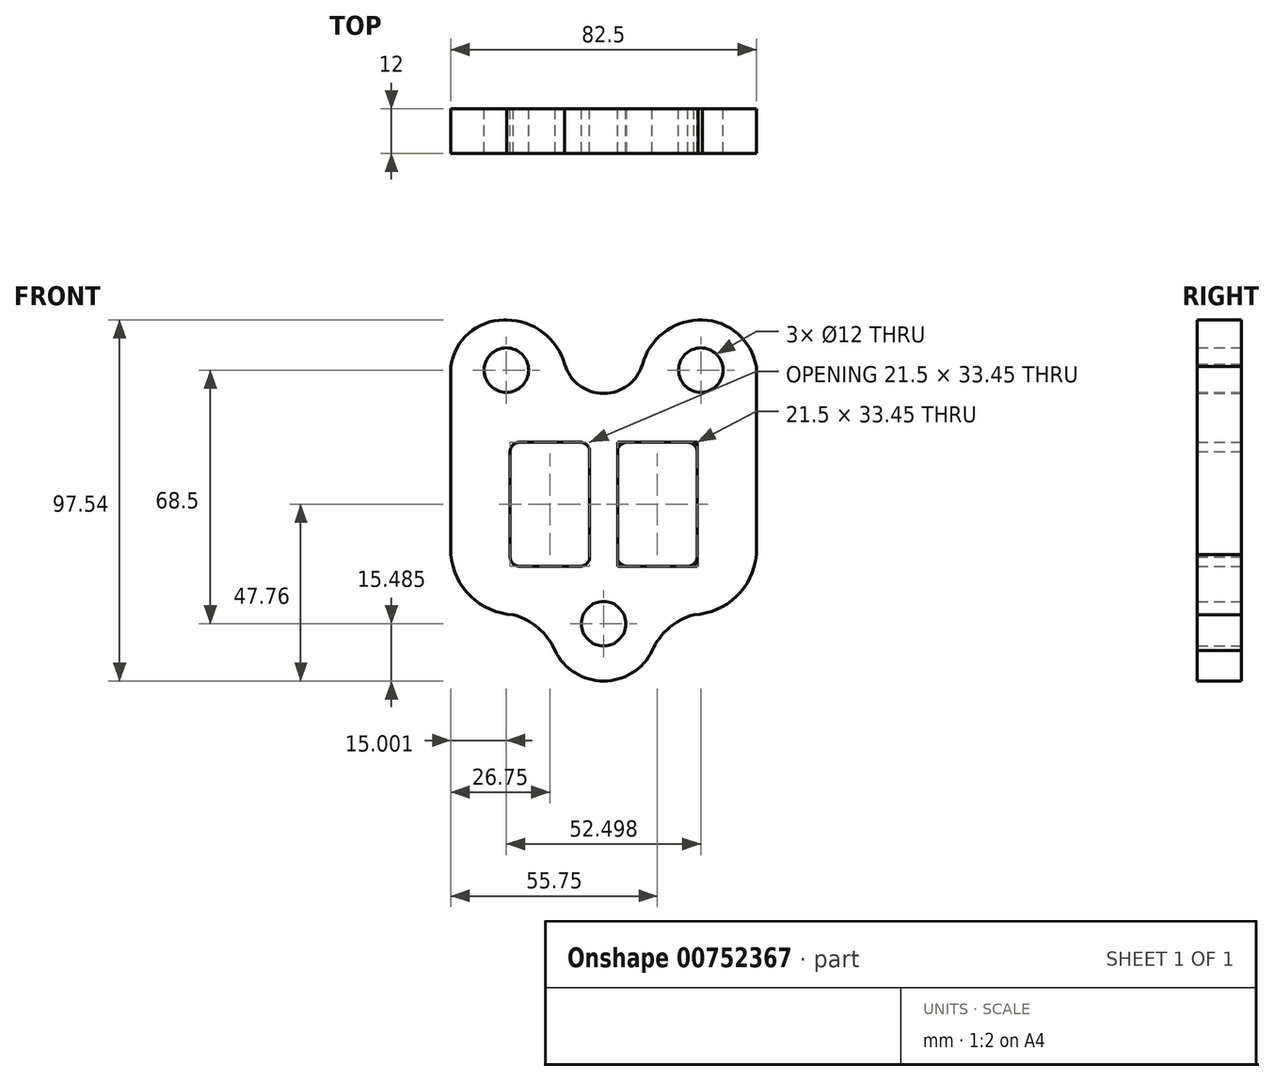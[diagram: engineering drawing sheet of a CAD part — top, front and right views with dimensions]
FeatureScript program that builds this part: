
annotation { "Feature Type Name" : "Feature", "Feature Type Description" : "" }
export const myFeature = defineFeature(function(context is Context, id is Id, definition is map)
    precondition{}
    {
        {
            var Q0;
            Q0=qCreatedBy(makeId("Front.planeOp"),FACE);
            var sketch = newSketch(context, id + "F0", { "sketchPlane" : qUnion([Q0])});
            skLineSegment(sketch, "E0.bottom", {"start": v(-41.25, 48.77) * mm, "end": v(41.25, 48.77) * mm});
            skLineSegment(sketch, "E0.top", {"start": v(-41.25, -48.77) * mm, "end": v(41.25, -48.77) * mm});
            skLineSegment(sketch, "E0.left", {"start": v(-41.25, 48.77) * mm, "end": v(-41.25, -48.77) * mm});
            skLineSegment(sketch, "E0.right", {"start": v(41.25, 48.77) * mm, "end": v(41.25, -48.77) * mm});
            skPoint(sketch, "E0.middle", {"position": v(0, 0) * mm});
            skLineSegment(sketch, "E1.bottom", {"start": v(-25.25, -17.73) * mm, "end": v(-3.75, -17.73) * mm});
            skLineSegment(sketch, "E1.top", {"start": v(-25.25, 15.72) * mm, "end": v(-3.75, 15.72) * mm});
            skLineSegment(sketch, "E1.left", {"start": v(-25.25, -17.73) * mm, "end": v(-25.25, 15.72) * mm});
            skLineSegment(sketch, "E1.right", {"start": v(-3.75, -17.73) * mm, "end": v(-3.75, 15.72) * mm});
            skLineSegment(sketch, "E2.bottom", {"start": v(3.75, -17.73) * mm, "end": v(25.25, -17.73) * mm});
            skLineSegment(sketch, "E2.top", {"start": v(3.75, 15.72) * mm, "end": v(25.25, 15.72) * mm});
            skLineSegment(sketch, "E2.left", {"start": v(3.75, -17.73) * mm, "end": v(3.75, 15.72) * mm});
            skLineSegment(sketch, "E2.right", {"start": v(25.25, -17.73) * mm, "end": v(25.25, 15.72) * mm});
            skCircle(sketch, "E3", {"center": v(-26.25, 35.22) * mm, "radius": 6 * mm});
            skCircle(sketch, "E4", {"center": v(26.25, 35.22) * mm, "radius": 6 * mm});
            skCircle(sketch, "E5", {"center": v(0, -33.28) * mm, "radius": 6 * mm});
            skSolve(sketch);
        }
        {
            var Q0;
            Q0=makeQuery(id+"F0.imprint","IMPRINT",FACE,{"disambiguationData":[TD([[makeQuery(id+"F0.imprint","IMPRINT",EDGE,{"derivedFrom":sQuery(id+"F0.wireOp",EDGE,"E0.bottom")}),-1.0]])]});
            var sketch = newSketch(context, id + "F1", { "sketchPlane" : qUnion([Q0])});
            skArc(sketch, "E6", {"start": v(-26.69, 48.77) * mm, "mid": v(-36.34, 45.2) * mm, "end": v(-41.25, 36.17) * mm});
            skArc(sketch, "E7", {"start": v(41.25, 36.17) * mm, "mid": v(36.2, 45.04) * mm, "end": v(26.69, 48.77) * mm});
            skSolve(sketch);
        }
        {
            var Q0;
            {var subQ5=sQuery(id+"F1.wireOp",EDGE,"E7");Q0=makeQuery(id+"F1.imprint","IMPRINT",FACE,{"disambiguationData":[TD([[makeQuery(id+"F1.imprint","IMPRINT",EDGE,{"derivedFrom":subQ5}),1.0]])]});}
            var sketch = newSketch(context, id + "F2", { "sketchPlane" : qUnion([Q0])});
            skArc(sketch, "E8", {"start": v(-10.48, 36.85) * mm, "mid": v(-16.56, 45.52) * mm, "end": v(-26.64, 48.77) * mm});
            skArc(sketch, "E9", {"start": v(27, 48.77) * mm, "mid": v(16.67, 45.67) * mm, "end": v(10.48, 36.85) * mm});
            skArc(sketch, "E10", {"start": v(-10.48, 36.85) * mm, "mid": v(0, 28.9) * mm, "end": v(10.48, 36.85) * mm});
            skSolve(sketch);
        }
        {
            var Q0;
            {var subQ16=sQuery(id+"F2.wireOp",EDGE,"E10");Q0=makeQuery(id+"F2.imprint","IMPRINT",FACE,{"disambiguationData":[TD([[makeQuery(id+"F2.imprint","IMPRINT",EDGE,{"derivedFrom":subQ16}),-1.0]])]});}
            var sketch = newSketch(context, id + "F3", { "sketchPlane" : qUnion([Q0])});
            skArc(sketch, "E11", {"start": v(-13.14, -40.5) * mm, "mid": v(0, -48.76) * mm, "end": v(13.14, -40.5) * mm});
            skArc(sketch, "E12", {"start": v(24.34, -30.82) * mm, "mid": v(35.87, -25.92) * mm, "end": v(41.25, -14.6) * mm});
            skArc(sketch, "E13", {"start": v(-41.25, -14.6) * mm, "mid": v(-35.87, -25.92) * mm, "end": v(-24.34, -30.82) * mm});
            skArc(sketch, "E14", {"start": v(24.34, -30.82) * mm, "mid": v(17.68, -34.43) * mm, "end": v(13.14, -40.5) * mm});
            skArc(sketch, "E15", {"start": v(-13.14, -40.5) * mm, "mid": v(-17.68, -34.43) * mm, "end": v(-24.34, -30.82) * mm});
            skSolve(sketch);
        }
        {
            var Q0;
            {var subQ4=sQuery(id+"F3.wireOp",EDGE,"E12");Q0=makeQuery(id+"F3.imprint","IMPRINT",FACE,{"disambiguationData":[TD([[makeQuery(id+"F3.imprint","IMPRINT",EDGE,{"derivedFrom":subQ4}),1.0]])]});}
            var sketch = newSketch(context, id + "F4", { "sketchPlane" : qUnion([Q0])});
            skArc(sketch, "E16", {"start": v(-22.75, 15.72) * mm, "mid": v(-24.52, 14.98) * mm, "end": v(-25.25, 13.22) * mm});
            skArc(sketch, "E17", {"start": v(-3.75, 13.22) * mm, "mid": v(-4.48, 14.98) * mm, "end": v(-6.25, 15.72) * mm});
            skArc(sketch, "E18", {"start": v(-25.25, -15.23) * mm, "mid": v(-24.52, -17) * mm, "end": v(-22.75, -17.73) * mm});
            skArc(sketch, "E19", {"start": v(-6.25, -17.73) * mm, "mid": v(-4.48, -17) * mm, "end": v(-3.75, -15.23) * mm});
            skSolve(sketch);
        }
        {
            var Q0;
            Q0=makeQuery(id+"F4.imprint","IMPRINT",FACE,{"disambiguationData":[TD([[makeQuery(id+"F4.imprint","IMPRINT",EDGE,{"derivedFrom":makeQuery(id+"F3.imprint","IMPRINT",EDGE,{"derivedFrom":makeQuery(id+"F2.imprint","IMPRINT",EDGE,{"derivedFrom":makeQuery(id+"F1.imprint","IMPRINT",EDGE,{"derivedFrom":makeQuery(id+"F0.imprint","IMPRINT",EDGE,{"derivedFrom":sQuery(id+"F0.wireOp",EDGE,"E2.bottom")})})})})}),1.0]])]});
            var sketch = newSketch(context, id + "F5", { "sketchPlane" : qUnion([Q0])});
            skArc(sketch, "E20", {"start": v(6.25, 15.72) * mm, "mid": v(4.48, 14.98) * mm, "end": v(3.75, 13.22) * mm});
            skArc(sketch, "E21", {"start": v(25.25, 13.22) * mm, "mid": v(24.52, 14.98) * mm, "end": v(22.75, 15.72) * mm});
            skArc(sketch, "E22", {"start": v(3.75, -15.23) * mm, "mid": v(4.48, -17) * mm, "end": v(6.25, -17.73) * mm});
            skArc(sketch, "E23", {"start": v(22.75, -17.73) * mm, "mid": v(24.52, -17) * mm, "end": v(25.25, -15.23) * mm});
            skSolve(sketch);
        }
        {
            var Q0;
            {var subQ15=sQuery(id+"F3.wireOp",EDGE,"E12");Q0=makeQuery(id+"F4.imprint","IMPRINT",FACE,{"disambiguationData":[TD([[makeQuery(id+"F4.imprint","IMPRINT",EDGE,{"derivedFrom":makeQuery(id+"F3.imprint","IMPRINT",EDGE,{"derivedFrom":subQ15})}),1.0]])]});}
            var Q1;
            {var subQ0=sQuery(id+"F5.wireOp",EDGE,"E22");Q1=makeQuery(id+"F5.imprint","IMPRINT",FACE,{"disambiguationData":[TD([[makeQuery(id+"F5.imprint","IMPRINT",EDGE,{"derivedFrom":subQ0}),-1.0]])]});}
            var Q2;
            {var subQ0=sQuery(id+"F5.wireOp",EDGE,"E20");Q2=makeQuery(id+"F5.imprint","IMPRINT",FACE,{"disambiguationData":[TD([[makeQuery(id+"F5.imprint","IMPRINT",EDGE,{"derivedFrom":subQ0}),-1.0]])]});}
            var Q3;
            {var subQ0=sQuery(id+"F5.wireOp",EDGE,"E23");Q3=makeQuery(id+"F5.imprint","IMPRINT",FACE,{"disambiguationData":[TD([[makeQuery(id+"F5.imprint","IMPRINT",EDGE,{"derivedFrom":subQ0}),-1.0]])]});}
            var Q4;
            {var subQ0=sQuery(id+"F5.wireOp",EDGE,"E21");Q4=makeQuery(id+"F5.imprint","IMPRINT",FACE,{"disambiguationData":[TD([[makeQuery(id+"F5.imprint","IMPRINT",EDGE,{"derivedFrom":subQ0}),-1.0]])]});}
            var Q5;
            {var subQ0=sQuery(id+"F4.wireOp",EDGE,"E19");Q5=makeQuery(id+"F4.imprint","IMPRINT",FACE,{"disambiguationData":[TD([[makeQuery(id+"F4.imprint","IMPRINT",EDGE,{"derivedFrom":subQ0}),-1.0]])]});}
            var Q6;
            {var subQ0=sQuery(id+"F4.wireOp",EDGE,"E16");Q6=makeQuery(id+"F4.imprint","IMPRINT",FACE,{"disambiguationData":[TD([[makeQuery(id+"F4.imprint","IMPRINT",EDGE,{"derivedFrom":subQ0}),-1.0]])]});}
            var Q7;
            {var subQ0=sQuery(id+"F4.wireOp",EDGE,"E18");Q7=makeQuery(id+"F4.imprint","IMPRINT",FACE,{"disambiguationData":[TD([[makeQuery(id+"F4.imprint","IMPRINT",EDGE,{"derivedFrom":subQ0}),-1.0]])]});}
            var Q8;
            {var subQ0=sQuery(id+"F4.wireOp",EDGE,"E17");Q8=makeQuery(id+"F4.imprint","IMPRINT",FACE,{"disambiguationData":[TD([[makeQuery(id+"F4.imprint","IMPRINT",EDGE,{"derivedFrom":subQ0}),-1.0]])]});}
            extrude(context, id + "F6", {"entities" : qUnion([Q0, Q1, Q2, Q3, Q4, Q5, Q6, Q7, Q8]), "depth" : 12 * mm, "offsetDistance" : 25 * mm});
        }
    });
